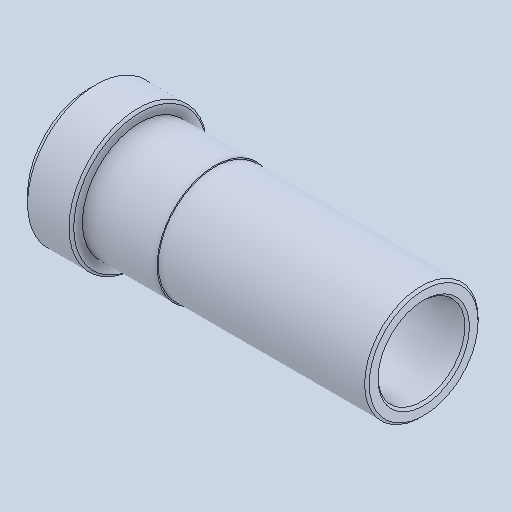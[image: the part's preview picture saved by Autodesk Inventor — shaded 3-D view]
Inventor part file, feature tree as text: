
AUTODESK INVENTOR PART (.ipt)
format: ipt  version: 2023.2 (Build 272271000, 271)  size: 144,896 bytes
history: native  units: in
note: dims shown in document units (in); Inventor stores cm internally (conversion verified against a paired STEP export)
features: chamfer x1
ambient origin geometry x8: Origin, YZ Plane, XZ Plane, XY Plane, X Axis, Y Axis, Z Axis, Center Point
bodies: Solid1 (feature_tree)
feature tree (1):
  chamfer  "Chamfer3"  [1 undecoded]
note: 1 required parameter value undecoded (feature->parameter linkage not recoverable at this tier; creation-order binding heuristic only, values carry confidence <= 0.55)
